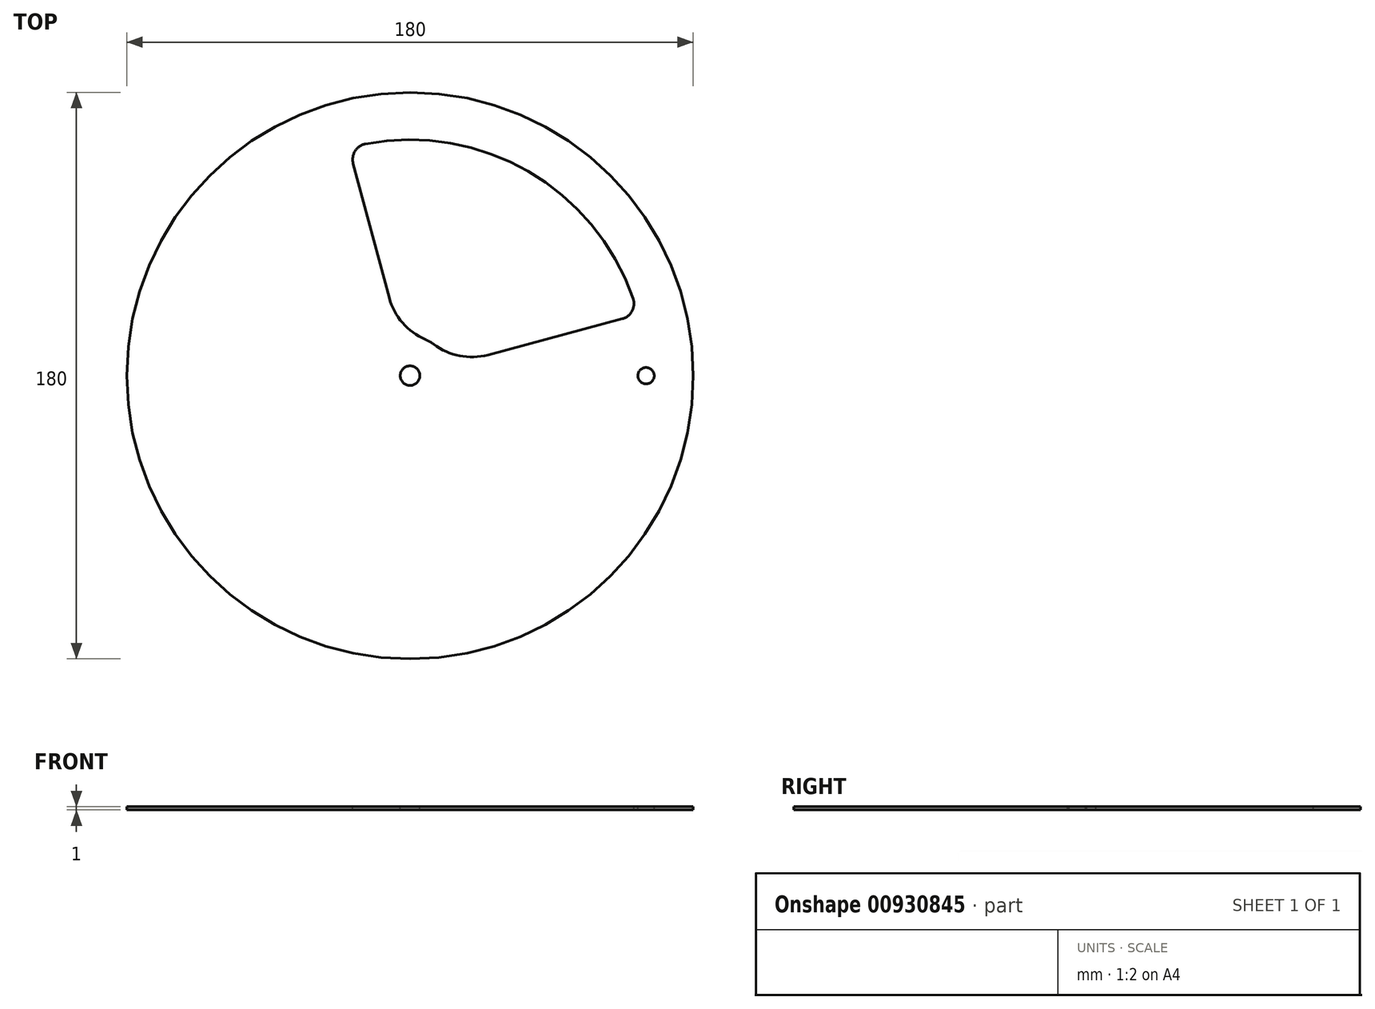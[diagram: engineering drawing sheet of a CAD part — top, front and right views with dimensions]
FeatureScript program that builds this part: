
annotation { "Feature Type Name" : "Feature", "Feature Type Description" : "" }
export const myFeature = defineFeature(function(context is Context, id is Id, definition is map)
    precondition{}
    {
        {
            var Q0;
            Q0=qCreatedBy(makeId("Top.planeOp"),FACE);
            var sketch = newSketch(context, id + "F0", { "sketchPlane" : qUnion([Q0])});
            skCircle(sketch, "E0", {"center": v(0, 0) * mm, "radius": 90 * mm});
            skCircle(sketch, "E1", {"center": v(0, 0) * mm, "radius": 3.1 * mm});
            skSolve(sketch);
        }
        {
            var Q0;
            Q0=makeQuery(id+"F0.imprint","IMPRINT",FACE,{"disambiguationData":[TD([[makeQuery(id+"F0.imprint","IMPRINT",EDGE,{"derivedFrom":sQuery(id+"F0.wireOp",EDGE,"E0")}),1.0]])]});
            extrude(context, id + "F1", {"entities" : qUnion([Q0]), "oppositeDirection" : true, "depth" : 1 * mm});
        }
        {
            var Q0;
            Q0=qCreatedBy(makeId("Top.planeOp"),FACE);
            var sketch = newSketch(context, id + "F2", { "sketchPlane" : qUnion([Q0])});
            skCircle(sketch, "E2", {"center": v(0, 0) * mm, "radius": 12.5 * mm});
            skCircle(sketch, "E3", {"center": v(0, 0) * mm, "radius": 75 * mm});
            skLineSegment(sketch, "E4", {"start": v(0, 0) * mm, "end": v(72.44, 19.41) * mm});
            skLineSegment(sketch, "E5", {"start": v(0, 0) * mm, "end": v(-19.41, 72.44) * mm});
            skSolve(sketch);
        }
        {
            var Q0;
            {var subQ0=sQuery(id+"F2.wireOp",EDGE,"E4");var subQ1=sQuery(id+"F2.wireOp",EDGE,"E2");var subQ2=makeQuery(id+"F2.imprint","INTERSECT",VERTEX,{"derivedFrom":[subQ1,subQ0]});Q0=makeQuery(id+"F2.imprint","IMPRINT",FACE,{"disambiguationData":[TD([[makeQuery(id+"F2.imprint","IMPRINT",EDGE,{"disambiguationData":[TD([[subQ2,-1.0]])],"derivedFrom":subQ1}),-1.0]])]});}
            extrude(context, id + "F3", {"entities" : qUnion([Q0]), "operationType" : NewBodyOperationType.REMOVE, "endBound" : BoundingType.SYMMETRIC, "oppositeDirection" : true, "offsetDistance" : 25 * mm, "depth" : 25 * mm});
        }
        {
            var Q0;
            Q0=qCreatedBy(makeId("Top.planeOp"),FACE);
            var sketch = newSketch(context, id + "F4", { "sketchPlane" : qUnion([Q0])});
            skCircle(sketch, "E6", {"center": v(75, 0) * mm, "radius": 2.6 * mm});
            skSolve(sketch);
        }
        {
            var Q0;
            Q0=makeQuery(id+"F4.imprint","IMPRINT",FACE,{"disambiguationData":[TD([[makeQuery(id+"F4.imprint","IMPRINT",EDGE,{"derivedFrom":sQuery(id+"F4.wireOp",EDGE,"E6")}),1.0]])]});
            extrude(context, id + "F5", {"entities" : qUnion([Q0]), "operationType" : NewBodyOperationType.REMOVE, "oppositeDirection" : true, "depth" : 25 * mm});
        }
        {
            var Q0;
            Q0=makeQuery(id+"F3.boolean.opBoolean","COPY",EDGE,{"derivedFrom":makeQuery(id+"F3.opExtrude","SWEPT_EDGE",EDGE,{"disambiguationData":[OSD([sQuery(id+"F2.wireOp",EDGE,"E3"),sQuery(id+"F2.wireOp",EDGE,"E5")])]})});
            var Q1;
            Q1=makeQuery(id+"FyyGSJt8pnxAcss_1.1.F3.boolean.opBoolean","COPY",EDGE,{"derivedFrom":makeQuery(id+"FyyGSJt8pnxAcss_1.1.F3.opExtrude","SWEPT_EDGE",EDGE,{"disambiguationData":[OSD([sQuery(id+"F2.wireOp",EDGE,"E3"),sQuery(id+"F2.wireOp",EDGE,"E4")])]})});
            var Q2;
            Q2=makeQuery(id+"FyyGSJt8pnxAcss_1.1.F3.boolean.opBoolean","COPY",EDGE,{"derivedFrom":makeQuery(id+"FyyGSJt8pnxAcss_1.1.F3.opExtrude","SWEPT_EDGE",EDGE,{"disambiguationData":[OSD([sQuery(id+"F2.wireOp",EDGE,"E3"),sQuery(id+"F2.wireOp",EDGE,"E5")])]})});
            var Q3;
            Q3=makeQuery(id+"FyyGSJt8pnxAcss_1.2.F3.boolean.opBoolean","COPY",EDGE,{"derivedFrom":makeQuery(id+"FyyGSJt8pnxAcss_1.2.F3.opExtrude","SWEPT_EDGE",EDGE,{"disambiguationData":[OSD([sQuery(id+"F2.wireOp",EDGE,"E3"),sQuery(id+"F2.wireOp",EDGE,"E4")])]})});
            var Q4;
            Q4=makeQuery(id+"FyyGSJt8pnxAcss_1.2.F3.boolean.opBoolean","COPY",EDGE,{"derivedFrom":makeQuery(id+"FyyGSJt8pnxAcss_1.2.F3.opExtrude","SWEPT_EDGE",EDGE,{"disambiguationData":[OSD([sQuery(id+"F2.wireOp",EDGE,"E3"),sQuery(id+"F2.wireOp",EDGE,"E5")])]})});
            var Q5;
            Q5=makeQuery(id+"F3.boolean.opBoolean","COPY",EDGE,{"derivedFrom":makeQuery(id+"F3.opExtrude","SWEPT_EDGE",EDGE,{"disambiguationData":[OSD([sQuery(id+"F2.wireOp",EDGE,"E3"),sQuery(id+"F2.wireOp",EDGE,"E4")])]})});
            fillet(context, id + "F6", {"entities" : qUnion([Q0, Q1, Q2, Q3, Q4, Q5]), "radius" : 5 * mm, "tangentPropagation" : true, "allowEdgeOverflow" : false});
        }
        {
            var Q0;
            Q0=makeQuery(id+"FyyGSJt8pnxAcss_1.1.F3.boolean.opBoolean","COPY",EDGE,{"derivedFrom":makeQuery(id+"FyyGSJt8pnxAcss_1.1.F3.opExtrude","SWEPT_EDGE",EDGE,{"disambiguationData":[OSD([sQuery(id+"F2.wireOp",EDGE,"E2"),sQuery(id+"F2.wireOp",EDGE,"E4")])]})});
            var Q1;
            Q1=makeQuery(id+"FyyGSJt8pnxAcss_1.1.F3.boolean.opBoolean","COPY",EDGE,{"derivedFrom":makeQuery(id+"FyyGSJt8pnxAcss_1.1.F3.opExtrude","SWEPT_EDGE",EDGE,{"disambiguationData":[OSD([sQuery(id+"F2.wireOp",EDGE,"E2"),sQuery(id+"F2.wireOp",EDGE,"E5")])]})});
            var Q2;
            Q2=makeQuery(id+"FyyGSJt8pnxAcss_1.2.F3.boolean.opBoolean","COPY",EDGE,{"derivedFrom":makeQuery(id+"FyyGSJt8pnxAcss_1.2.F3.opExtrude","SWEPT_EDGE",EDGE,{"disambiguationData":[OSD([sQuery(id+"F2.wireOp",EDGE,"E2"),sQuery(id+"F2.wireOp",EDGE,"E4")])]})});
            var Q3;
            Q3=makeQuery(id+"FyyGSJt8pnxAcss_1.2.F3.boolean.opBoolean","COPY",EDGE,{"derivedFrom":makeQuery(id+"FyyGSJt8pnxAcss_1.2.F3.opExtrude","SWEPT_EDGE",EDGE,{"disambiguationData":[OSD([sQuery(id+"F2.wireOp",EDGE,"E2"),sQuery(id+"F2.wireOp",EDGE,"E5")])]})});
            var Q4;
            Q4=makeQuery(id+"F3.boolean.opBoolean","COPY",EDGE,{"derivedFrom":makeQuery(id+"F3.opExtrude","SWEPT_EDGE",EDGE,{"disambiguationData":[OSD([sQuery(id+"F2.wireOp",EDGE,"E2"),sQuery(id+"F2.wireOp",EDGE,"E4")])]})});
            var Q5;
            Q5=makeQuery(id+"F3.boolean.opBoolean","COPY",EDGE,{"derivedFrom":makeQuery(id+"F3.opExtrude","SWEPT_EDGE",EDGE,{"disambiguationData":[OSD([sQuery(id+"F2.wireOp",EDGE,"E2"),sQuery(id+"F2.wireOp",EDGE,"E5")])]})});
            fillet(context, id + "F7", {"entities" : qUnion([Q0, Q1, Q2, Q3, Q4, Q5]), "radius" : 20 * mm, "tangentPropagation" : true, "allowEdgeOverflow" : false});
        }
    });
